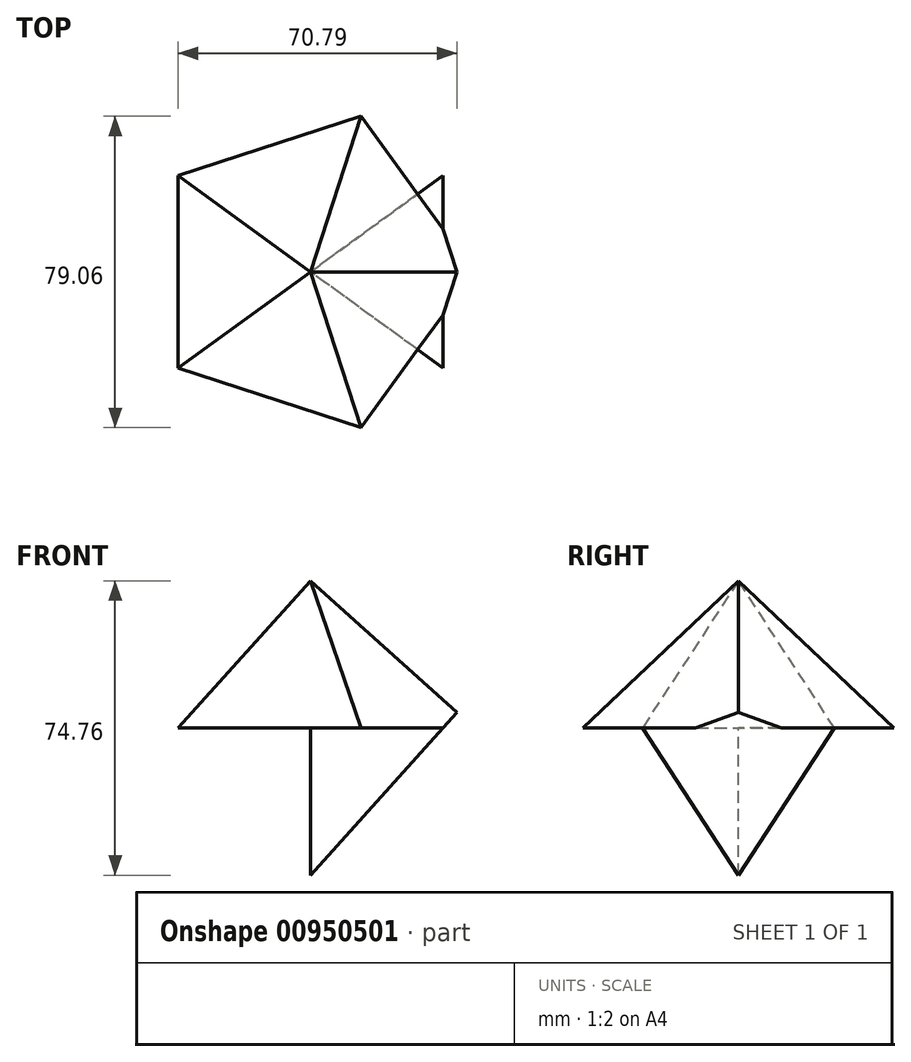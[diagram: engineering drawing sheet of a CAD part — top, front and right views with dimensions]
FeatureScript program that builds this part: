
annotation { "Feature Type Name" : "Feature", "Feature Type Description" : "" }
export const myFeature = defineFeature(function(context is Context, id is Id, definition is map)
    precondition{}
    {
        {
            var Q0;
            Q0=qCreatedBy(makeId("Front.planeOp"),FACE);
            var sketch = newSketch(context, id + "F0", { "sketchPlane" : qUnion([Q0])});
            skLineSegment(sketch, "E0", {"start": v(-33.62, 0) * mm, "end": v(0, 37.38) * mm, "construction": true});
            skLineSegment(sketch, "E1", {"start": v(0, 37.38) * mm, "end": v(0, 0) * mm, "construction": true});
            skLineSegment(sketch, "E2", {"start": v(0, 37.38) * mm, "end": v(41.56, 0) * mm, "construction": true});
            skCircle(sketch, "E3.cCircle", {"center": v(0, 0) * mm, "radius": 33.62 * mm, "construction": true});
            skLineSegment(sketch, "E3.0", {"start": v(-33.62, -24.43) * mm, "end": v(-33.62, 24.43) * mm, "construction": true});
            skLineSegment(sketch, "E3.1", {"start": v(-33.62, 24.43) * mm, "end": v(12.84, 39.53) * mm, "construction": true});
            skLineSegment(sketch, "E3.2", {"start": v(12.84, 39.53) * mm, "end": v(41.56, 0) * mm, "construction": true});
            skLineSegment(sketch, "E3.3", {"start": v(41.56, 0) * mm, "end": v(12.84, -39.53) * mm, "construction": true});
            skLineSegment(sketch, "E3.4", {"start": v(12.84, -39.53) * mm, "end": v(-33.62, -24.43) * mm, "construction": true});
            skPoint(sketch, "E3.0.midPoint", {"position": v(-33.62, 0) * mm});
            skLineSegment(sketch, "E4", {"start": v(0, 0) * mm, "end": v(0, -37.38) * mm, "construction": true});
            skSolve(sketch);
        }
        {
            var Q0;
            Q0=qCreatedBy(makeId("Top.planeOp"),FACE);
            var sketch = newSketch(context, id + "F1", { "sketchPlane" : qUnion([Q0])});
            skCircle(sketch, "E5.cCircle", {"center": v(0, 0) * mm, "radius": 33.62 * mm, "construction": true});
            skLineSegment(sketch, "E5.0", {"start": v(-33.62, -24.43) * mm, "end": v(-33.62, 24.43) * mm, "construction": true});
            skLineSegment(sketch, "E5.1", {"start": v(-33.62, 24.43) * mm, "end": v(12.84, 39.53) * mm, "construction": true});
            skLineSegment(sketch, "E5.2", {"start": v(12.84, 39.53) * mm, "end": v(41.56, 0) * mm, "construction": true});
            skLineSegment(sketch, "E5.3", {"start": v(41.56, 0) * mm, "end": v(12.84, -39.53) * mm, "construction": true});
            skLineSegment(sketch, "E5.4", {"start": v(12.84, -39.53) * mm, "end": v(-33.62, -24.43) * mm, "construction": true});
            skPoint(sketch, "E5.0.midPoint", {"position": v(-33.62, 0) * mm});
            skLineSegment(sketch, "E6.0", {"start": v(33.62, 24.43) * mm, "end": v(33.62, -24.43) * mm, "construction": true});
            skLineSegment(sketch, "E6.1", {"start": v(33.62, -24.43) * mm, "end": v(-12.84, -39.53) * mm, "construction": true});
            skLineSegment(sketch, "E6.2", {"start": v(-12.84, -39.53) * mm, "end": v(-41.56, 0) * mm, "construction": true});
            skLineSegment(sketch, "E6.3", {"start": v(-41.56, 0) * mm, "end": v(-12.84, 39.53) * mm, "construction": true});
            skLineSegment(sketch, "E6.4", {"start": v(-12.84, 39.53) * mm, "end": v(33.62, 24.43) * mm, "construction": true});
            skPoint(sketch, "E6.0.midPoint", {"position": v(33.62, 0) * mm});
            skSolve(sketch);
        }
        {
            var Q0;
            Q0=sQuery(id+"F0.wireOp",VERTEX,"E0.end");
            var Q1;
            Q1=sQuery(id+"F1.wireOp",VERTEX,"E5.0.end");
            var Q2;
            Q2=sQuery(id+"F1.wireOp",VERTEX,"E5.0.start");
            cPlane(context, id + "F2", {"entities" : qUnion([Q0, Q1, Q2]), "cplaneType" : CPlaneType.THREE_POINT, "offset" : 25 * mm, "width" : 150 * mm, "height" : 150 * mm});
        }
        {
            var Q0;
            Q0=qCreatedBy(id+"F2.planeOp",FACE);
            var sketch = newSketch(context, id + "F3", { "sketchPlane" : qUnion([Q0])});
            skLineSegment(sketch, "E7.0", {"start": v(-24.43, -22.49) * mm, "end": v(24.43, -22.49) * mm});
            skLineSegment(sketch, "E8", {"start": v(24.43, -22.49) * mm, "end": v(0, 27.8) * mm});
            skLineSegment(sketch, "E9", {"start": v(0, 27.8) * mm, "end": v(-24.43, -22.49) * mm});
            skSolve(sketch);
        }
        {
            var Q0;
            Q0=makeQuery(id+"F3.imprint","IMPRINT",FACE,{"disambiguationData":[TD([[makeQuery(id+"F3.imprint","IMPRINT",EDGE,{"derivedFrom":sQuery(id+"F3.wireOp",EDGE,"E7.0")}),1.0]])]});
            var Q1;
            Q1=qCreatedBy(makeId("Origin.pointOp"),VERTEX);
            loft(context, id + "F4", {"sheetProfilesArray" : [{ "sheetProfileEntities" : qUnion([Q0]) }, { "sheetProfileEntities" : qUnion([Q1]) }]});
        }
        {
            var Q0;
            Q0=makeQuery(id+"F4.opLoft","SWEPT_BODY",BODY,{"disambiguationData":[OSD([dummyQuery(id+"Origin.pointOp",VERTEX),makeQuery(id+"F3.imprint","IMPRINT",FACE,{"disambiguationData":[TD([[makeQuery(id+"F3.imprint","IMPRINT",EDGE,{"derivedFrom":sQuery(id+"F3.wireOp",EDGE,"E7.0")}),1.0]])]})])]});
            var Q1;
            Q1=sQuery(id+"F0.wireOp",EDGE,"E1");
            circularPattern(context, id + "F5", {"operationType" : NewBodyOperationType.ADD, "entities" : qUnion([Q0]), "axis" : qUnion([Q1]), "angle" : 360 * degree, "instanceCount" : 5, "equalSpace" : true});
        }
        {
            var Q0;
            Q0=sQuery(id+"F1.wireOp",VERTEX,"E6.0.end");
            var Q1;
            Q1=sQuery(id+"F1.wireOp",VERTEX,"E6.0.start");
            var Q2;
            Q2=sQuery(id+"F0.wireOp",VERTEX,"E4.end");
            cPlane(context, id + "F6", {"entities" : qUnion([Q0, Q1, Q2]), "cplaneType" : CPlaneType.THREE_POINT, "offset" : 25 * mm, "width" : 150 * mm, "height" : 150 * mm});
        }
        {
            var Q0;
            Q0=qCreatedBy(id+"F6.planeOp",FACE);
            var sketch = newSketch(context, id + "F7", { "sketchPlane" : qUnion([Q0])});
            skLineSegment(sketch, "E10.0", {"start": v(24.43, 22.49) * mm, "end": v(-24.43, 22.49) * mm});
            skLineSegment(sketch, "E11", {"start": v(-24.43, 22.49) * mm, "end": v(0, -27.8) * mm});
            skLineSegment(sketch, "E12", {"start": v(0, -27.8) * mm, "end": v(24.43, 22.49) * mm});
            skSolve(sketch);
        }
        {
            var Q1;
            Q1=makeQuery(id+"F7.imprint","IMPRINT",FACE,{"disambiguationData":[TD([[makeQuery(id+"F7.imprint","IMPRINT",EDGE,{"derivedFrom":sQuery(id+"F7.wireOp",EDGE,"E10.0")}),1.0]])]});
            var Q2;
            Q2=sQuery(id+"F0.wireOp",VERTEX,"E1.end");
            loft(context, id + "F8", {"operationType" : NewBodyOperationType.ADD, "sheetProfilesArray" : [{ "sheetProfileEntities" : qUnion([Q1]) }, { "sheetProfileEntities" : qUnion([Q2]) }]});
        }
        {
            var Q0;
            Q0=makeQuery(id+"F4.opLoft","CAP_FACE",FACE,{"disambiguationData":[OSD([makeQuery(id+"F3.imprint","IMPRINT",FACE,{"disambiguationData":[TD([[makeQuery(id+"F3.imprint","IMPRINT",EDGE,{"derivedFrom":sQuery(id+"F3.wireOp",EDGE,"E7.0")}),1.0]])]})])],"isStart":true});
            var sketch = newSketch(context, id + "F9", { "sketchPlane" : qUnion([Q0])});
            skLineSegment(sketch, "E13", {"start": v(-27, -27.8) * mm, "end": v(0, 27.8) * mm});
            skLineSegment(sketch, "E14", {"start": v(0, 27.8) * mm, "end": v(27, -27.8) * mm});
            skLineSegment(sketch, "E15", {"start": v(27, -27.8) * mm, "end": v(-27, -27.8) * mm});
            skSolve(sketch);
        }
        {
            var Q0;
            {var subQ21=sQuery(id+"F9.wireOp",EDGE,"E14");var subQ23=sQuery(id+"F9.wireOp",EDGE,"E13");var subQ24=makeQuery(id+"F9.imprint","INTERSECT",VERTEX,{"derivedFrom":[subQ23,subQ21]});Q0=makeQuery(id+"F9.imprint","IMPRINT",FACE,{"disambiguationData":[TD([[makeQuery(id+"F9.imprint","IMPRINT",EDGE,{"disambiguationData":[TD([[subQ24,-1.0]])],"derivedFrom":subQ21}),-1.0]])]});}
            var Q1;
            {var subQ21=sQuery(id+"F9.wireOp",EDGE,"E15");Q1=makeQuery(id+"F9.imprint","IMPRINT",FACE,{"disambiguationData":[TD([[makeQuery(id+"F9.imprint","IMPRINT",EDGE,{"derivedFrom":subQ21}),-1.0]])]});}
            extrude(context, id + "F10", {"entities" : qUnion([Q0, Q1]), "operationType" : NewBodyOperationType.REMOVE, "depth" : 25 * mm, "offsetDistance" : 25 * mm});
        }
        {
            var Q0;
            Q0=makeQuery(id+"F8.opLoft","CAP_FACE",FACE,{"disambiguationData":[OSD([makeQuery(id+"F7.imprint","IMPRINT",FACE,{"disambiguationData":[TD([[makeQuery(id+"F7.imprint","IMPRINT",EDGE,{"derivedFrom":sQuery(id+"F7.wireOp",EDGE,"E10.0")}),1.0]])]})])],"isStart":true});
            var sketch = newSketch(context, id + "F11", { "sketchPlane" : qUnion([Q0])});
            skLineSegment(sketch, "E16", {"start": v(-27, 27.8) * mm, "end": v(0, -27.8) * mm});
            skLineSegment(sketch, "E17", {"start": v(0, -27.8) * mm, "end": v(27, 27.8) * mm});
            skLineSegment(sketch, "E18", {"start": v(27, 27.8) * mm, "end": v(-27, 27.8) * mm});
            skSolve(sketch);
        }
        {
            var Q0;
            {var subQ0=sQuery(id+"F11.wireOp",EDGE,"E18");Q0=makeQuery(id+"F11.imprint","IMPRINT",FACE,{"disambiguationData":[TD([[makeQuery(id+"F11.imprint","IMPRINT",EDGE,{"derivedFrom":subQ0}),1.0]])]});}
            var Q1;
            {var subQ4=sQuery(id+"F7.wireOp",EDGE,"E10.0");var subQ5=makeQuery(id+"F7.imprint","IMPRINT",EDGE,{"derivedFrom":subQ4});var subQ8=makeQuery(id+"F8.opLoft","CAP_FACE",FACE,{"disambiguationData":[OSD([makeQuery(id+"F7.imprint","IMPRINT",FACE,{"disambiguationData":[TD([[subQ5,1.0]])]})])],"isStart":true});var subQ12=sQuery(id+"F9.wireOp",EDGE,"E15");var subQ13=sQuery(id+"F9.wireOp",EDGE,"E14");var subQ14=sQuery(id+"F9.wireOp",EDGE,"E13");var subQ15=makeQuery(id+"FLSPnottfK7hvsf_1.2.F10.boolean.opBoolean","INTERSECT",EDGE,{"derivedFrom":[subQ8,makeQuery(id+"FLSPnottfK7hvsf_1.2.F10.opExtrude","CAP_FACE",FACE,{"disambiguationData":[OSD([subQ14,subQ13,subQ12])],"isStart":true})]});Q1=makeQuery(id+"F11.imprint","IMPRINT",FACE,{"disambiguationData":[TD([[makeQuery(id+"F11.imprint","IMPRINT",EDGE,{"derivedFrom":subQ15}),1.0]])]});}
            extrude(context, id + "F12", {"entities" : qUnion([Q0, Q1]), "operationType" : NewBodyOperationType.REMOVE, "depth" : 25 * mm, "offsetDistance" : 25 * mm});
        }
    });
